# Revit family: Specialty_Door-Acudor-Walk_Through-WD-8000_Series
name_source: partatom
category: Specialty Equipment
revit_build: Autodesk Revit 2014 (Build: 20130308_1515(x64)
units: mm (PartAtom-declared; Revit-internal decimal feet)

## types (8) — shared parameters
Assembly Code = C1020700
Description = Walk Through Duct & Specialty Door
Finish = Galvanized Steel-Acudor-22 Gauge-Mill Finish
Installation Type = Surface Mount
Length = 1 5/8"
Manufacturer = Acudor
Material = Galvanized Steel-Acudor-22 Gauge-Mill Finish
Product Documentation Link = https://acudor.com
Product Page URL = https://acudor.com
Revised Date = 08/30/2018
URL = http://acudor.com

## per-type parameters (varying)
| type | 3 Latch | Default Elevation | Height | Width |
| WD-8000 24x36 | No | 38" | 36" | 24" |
| WD-8000 24x48 | Yes | 44" | 48" | 24" |
| WD-8000 24x60 | Yes | 50" | 60" | 24" |
| WD-8000 24x72 | Yes | 56" | 72" | 24" |
| WD-8000 30x36 | No | 38" | 36" | 30" |
| WD-8000 30x48 | Yes | 44" | 48" | 30" |
| WD-8000 30x60 | Yes | 50" | 60" | 30" |
| WD-8000 30x72 | Yes | 56" | 72" | 30" |

note: column(s) folded — value = type name in every type: Model

## geometry (parser evidence)
native form markers: Sweep x4
no freeform markers — native parametric forms only
